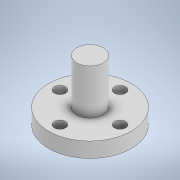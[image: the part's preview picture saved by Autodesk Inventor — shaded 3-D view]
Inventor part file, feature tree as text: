
AUTODESK INVENTOR PART (.ipt)
format: ipt  version: 2021 (Build 250183000, 183)  size: 121,344 bytes
history: native  units: mm
features: extrude x3, sketch x3, other x1
ambient origin geometry x8: Origin, YZ Plane, XZ Plane, XY Plane, X Axis, Y Axis, Z Axis, Center Point
bodies: Body1 (feature_tree)
feature tree (7):
  other  "Sólido1"
  extrude  "Extrusión1"  Depth=4.0mm TaperAngle=0.0deg
  extrude  "Extrusión2"  Depth=16.0mm
  extrude  "Extrusión3"  Depth=4.0mm TaperAngle=0.0deg
  sketch  "Boceto1"  dims[d0=22.0mm d1=4.0mm d2=0.0mm]
  sketch  "Boceto2"  dims[d3=16.0mm d4=3.0mm]
  sketch  "Boceto3"  dims[d5=40.0mm d7=360.0deg d9=4.0mm d10=0.0mm d11=7.0mm d12=12.0mm d13=0.0mm]
